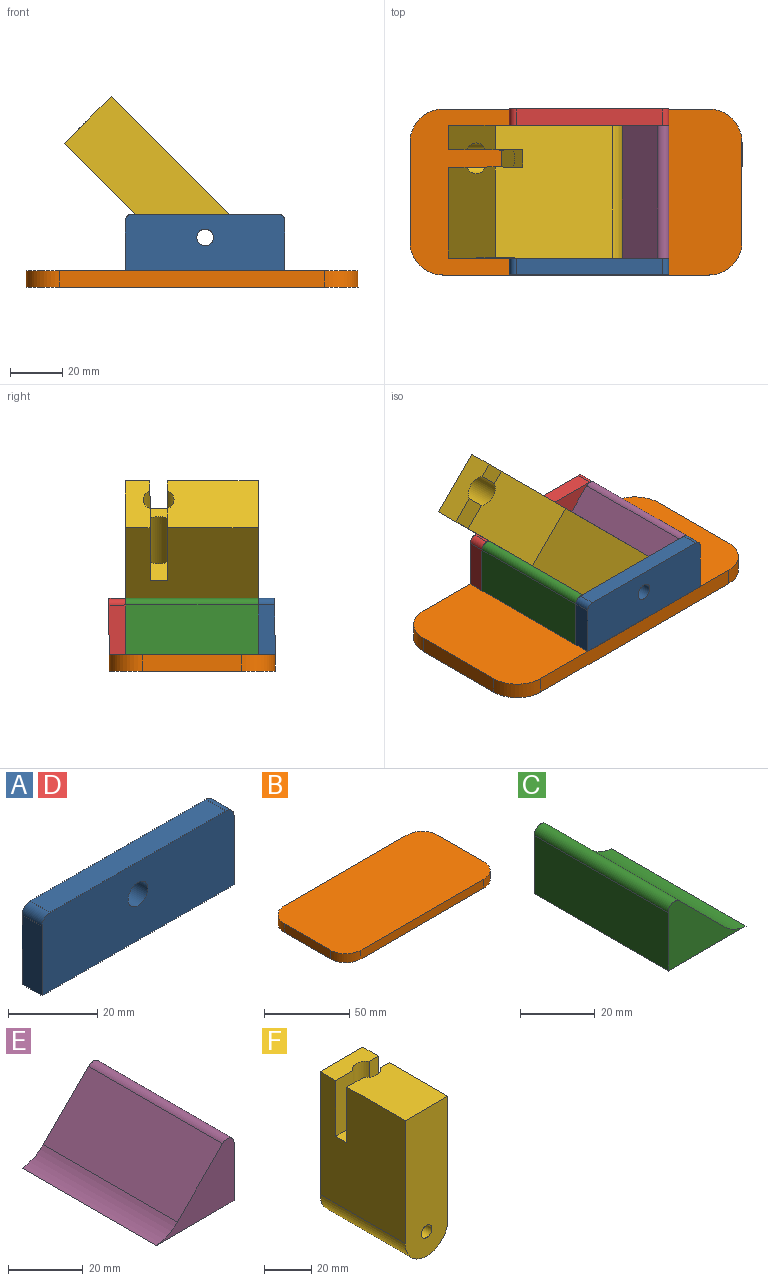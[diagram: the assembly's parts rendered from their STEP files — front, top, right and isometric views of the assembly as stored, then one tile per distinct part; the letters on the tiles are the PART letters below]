
ASSEMBLY  parts=6 mates=14
PART A: 9 faces, bbox 61x6.4x21.6 mm
  f0: plane 19.05x6.35mm, normal (-1,0,0), area 121mm2, adj f1,f5,f6,f7
  f1: plane 60.96x6.35mm, normal (0,0,-1), area 387.1mm2, adj f0,f2,f6,f7
  f2: plane 19.05x6.35mm, normal (1,0,0), area 121mm2, adj f1,f3,f6,f7
  f3: cylinder r=2.54mm len=6.35mm, axis (0,1,0), area 25.3mm2, adj f2,f4,f6,f7
  f4: plane 55.88x6.35mm, normal (0,0,1), area 354.8mm2, adj f3,f5,f6,f7
  f5: cylinder r=2.54mm len=6.35mm, axis (0,1,0), area 25.3mm2, adj f0,f4,f6,f7
  f6: plane 60.96x21.59mm, normal (0,-1,0), area 1281.7mm2, adj f0,f1,f2,f3,f4,f5,f8
  f7: plane 60.96x21.59mm, normal (0,1,0), area 1281.7mm2, adj f0,f1,f2,f3,f4,f5,f8
  f8: cylinder r=3.17mm len=6.35mm, axis (0,-1,0), area 126.7mm2, adj f6,f7
PART B: 10 faces, bbox 127x63.5x6.4 mm
  f0: plane 38.1x6.35mm, normal (1,0,0), area 241.9mm2, adj f1,f7,f8,f9
  f1: cylinder r=12.7mm len=12.7mm, axis (0,0,1), area 126.7mm2, adj f0,f2,f8,f9
  f2: plane 101.6x6.35mm, normal (0,1,0), area 645.2mm2, adj f1,f3,f8,f9
  f3: cylinder r=12.7mm len=12.7mm, axis (0,0,1), area 126.7mm2, adj f2,f4,f8,f9
  f4: plane 38.1x6.35mm, normal (-1,0,0), area 241.9mm2, adj f3,f5,f8,f9
  f5: cylinder r=12.7mm len=12.7mm, axis (0,0,1), area 126.7mm2, adj f4,f6,f8,f9
  f6: plane 101.6x6.35mm, normal (0,-1,0), area 645.2mm2, adj f5,f7,f8,f9
  f7: cylinder r=12.7mm len=12.7mm, axis (0,0,1), area 126.7mm2, adj f0,f6,f8,f9
  f8: plane 127x63.5mm, normal (0,0,-1), area 7926mm2, adj f0,f1,f2,f3,f4,f5,f6,f7
  f9: plane 127x63.5mm, normal (0,0,1), area 7926mm2, adj f0,f1,f2,f3,f4,f5,f6,f7
PART C: 7 faces, bbox 29.5x50.8x21.6 mm
  f0: cylinder r=12.7mm len=50.8mm, axis (0,-1,0), area 457.2mm2, adj f1,f4,f5,f6
  f1: plane 50.8x17.16mm, normal (0.71,0,0.71), area 1233.1mm2, adj f0,f2,f5,f6
  f2: cylinder r=2.54mm len=50.8mm, axis (0,-1,0), area 304mm2, adj f1,f3,f5,f6
  f3: plane 50.8x19.05mm, normal (-1,0,0), area 967.7mm2, adj f2,f4,f5,f6
  f4: plane 50.8x29.51mm, normal (0,0,-1), area 1498.9mm2, adj f0,f3,f5,f6
  f5: plane 29.51x21.59mm, normal (0,1,0), area 312.4mm2, adj f0,f1,f2,f3,f4
  f6: plane 29.51x21.59mm, normal (0,-1,0), area 312.4mm2, adj f0,f1,f2,f3,f4
PART D: same geometry as A
PART E: 7 faces, bbox 29.5x50.8x21.6 mm
  f0: cylinder r=12.7mm len=50.8mm, axis (0,-1,0), area 457.2mm2, adj f1,f4,f5,f6
  f1: plane 50.8x29.51mm, normal (0,0,-1), area 1498.9mm2, adj f0,f2,f5,f6
  f2: plane 50.8x19.05mm, normal (1,0,0), area 967.7mm2, adj f1,f3,f5,f6
  f3: cylinder r=2.54mm len=50.8mm, axis (0,-1,0), area 304mm2, adj f2,f4,f5,f6
  f4: plane 50.8x17.16mm, normal (-0.71,0,0.71), area 1233.1mm2, adj f0,f3,f5,f6
  f5: plane 29.51x21.59mm, normal (0,1,0), area 312.4mm2, adj f0,f1,f2,f3,f4
  f6: plane 29.51x21.59mm, normal (0,-1,0), area 312.4mm2, adj f0,f1,f2,f3,f4
PART F: 16 faces, bbox 25.4x50.8x76.2 mm
  f0: plane 25.4x9.4mm, normal (0,0,1), area 220.6mm2, adj f2,f4,f5,f8,f10,f14
  f1: plane 34.8x25.4mm, normal (0,0,1), area 865.8mm2, adj f2,f4,f6,f7,f11,f14
  f2: plane 63.5x50.8mm, normal (-1,0,0), area 3036.3mm2, adj f0,f1,f3,f5,f6,f10,f11,f12
  f3: cylinder r=12.7mm len=50.8mm, axis (0,-1,0), area 2026.8mm2, adj f2,f4,f5,f6
  f4: plane 63.5x50.8mm, normal (1,0,0), area 3126.8mm2, adj f0,f1,f3,f5,f6,f7,f8,f9
  f5: plane 76.2x25.4mm, normal (0,1,0), area 1834.6mm2, adj f0,f2,f3,f4,f13
  f6: plane 76.2x25.4mm, normal (0,-1,0), area 1834.6mm2, adj f1,f2,f3,f4,f13
  f7: plane 14.99x5.38mm, normal (0,1,0), area 80.6mm2, adj f1,f4,f9,f14
  f8: plane 14.99x5.38mm, normal (0,-1,0), area 80.6mm2, adj f0,f4,f9,f14
  f9: plane 6.6x5.38mm, normal (0,0,1), area 31mm2, adj f4,f7,f8,f14
  f10: plane 28.7x10.2mm, normal (0,-1,0), area 292.8mm2, adj f0,f2,f12,f14
  f11: plane 28.7x10.2mm, normal (0,1,0), area 292.8mm2, adj f1,f2,f12,f14
  f12: plane 10.2x6.6mm, normal (0,0,1), area 62.9mm2, adj f2,f10,f11,f14
  f13: cylinder r=3.17mm len=50.8mm, axis (0,-1,0), area 1013.4mm2, adj f5,f6
  f14: cylinder r=5.92mm len=50.8mm, axis (0,0,1), area 1582.9mm2, adj f0,f1,f7,f8,f9,f10,f11,f12
  f15: plane 11.84x11.84mm, normal (0,0,1), area 110mm2, adj f14
PLACE A rot(axis=(-1,0,0),0.1deg) t=(45.31,-133.7,11.62)mm
PLACE B rot(axis=(-1,0,0),0.1deg) t=(73.31,-140.05,11.62)mm
PLACE C rot(axis=(-1,0,0),0.1deg) t=(78.33,-140.05,11.59)mm
PLACE D rot(axis=(-1,0,0),0.1deg) t=(45.31,-76.55,11.55)mm
PLACE E rot(axis=(-1,0,0),0.1deg) t=(78.33,-140.05,11.59)mm
PLACE F rot(axis=(0,-1,0),45deg) t=(50.75,-133.67,42.28)mm
MATE planar D.f7 <-> B.f2  axis (0,1,0) through (14.83,-76.54,22.27)mm
MATE planar A.f1 <-> D.f1  axis (0,0,-1) through (14.83,-133.7,11.62)mm
MATE planar B.f3 <-> D.f1  axis (0,0,1) through (-40.99,-89.25,11.56)mm
MATE planar C.f5 <-> D.f6  axis (0,1,0) through (-6.89,-82.89,19.51)mm
MATE cylindrical F.f3 <-> A.f8  axis (0,-1,0) through (14.83,-133.69,24.32)mm
MATE planar A.f7 <-> F.f3  axis (0,1,0) through (14.83,-133.69,22.34)mm
MATE planar F.f5 <-> D.f6  axis (0,1,0) through (-4.38,-82.87,43.47)mm
MATE planar E.f1 <-> B.f9  axis (0,0,-1) through (30.55,-108.3,11.59)mm
MATE planar C.f4 <-> B.f9  axis (0,0,-1) through (-0.9,-108.3,11.59)mm
MATE planar E.f2 <-> D.f2  axis (1,0,0) through (45.31,-108.29,21.11)mm
MATE planar C.f3 <-> D.f0  axis (-1,0,0) through (-15.65,-108.29,21.11)mm
MATE cylindrical F.f3 <-> D.f8  axis (0,-1,0) through (14.83,-82.89,24.25)mm
MATE planar A.f6 <-> B.f6  axis (0,-1,0) through (14.83,-140.04,22.35)mm
MATE planar D.f3 <-> E.f5  axis (0,-1,0) through (42.77,-82.88,30.6)mm
